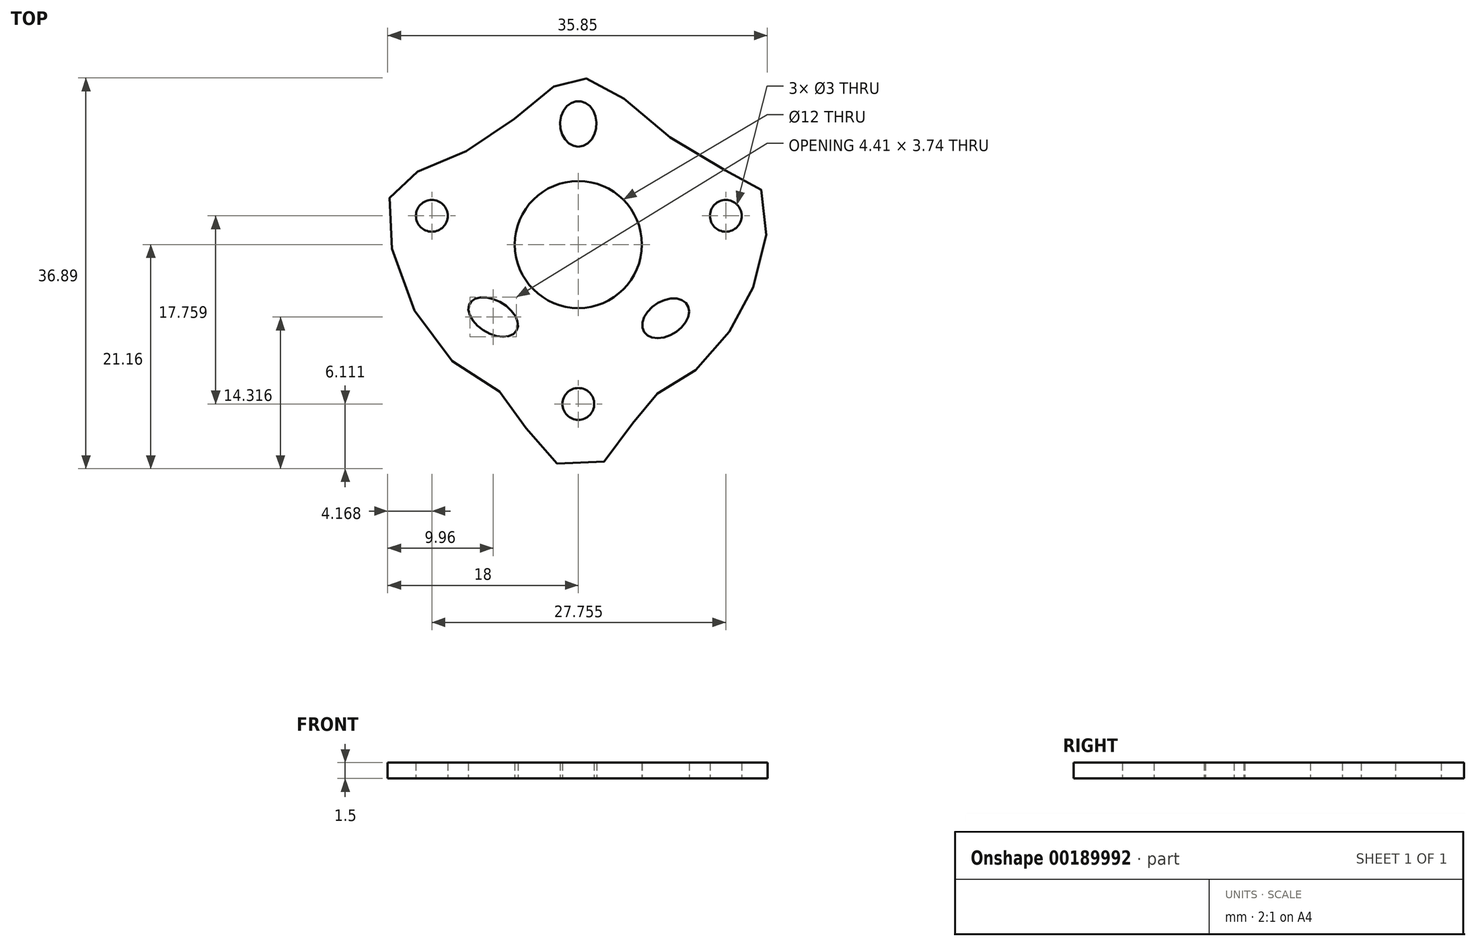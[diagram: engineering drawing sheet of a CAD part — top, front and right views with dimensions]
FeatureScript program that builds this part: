
annotation { "Feature Type Name" : "Feature", "Feature Type Description" : "" }
export const myFeature = defineFeature(function(context is Context, id is Id, definition is map)
    precondition{}
    {
        {
            var Q0;
            Q0=qCreatedBy(makeId("Top.planeOp"),FACE);
            var sketch = newSketch(context, id + "F0", { "sketchPlane" : qUnion([Q0])});
            skPoint(sketch, "E0", {"position": v(-6.76, 11.3) * mm});
            skPoint(sketch, "E1", {"position": v(-2.33, 14.92) * mm});
            skPoint(sketch, "E2", {"position": v(0, 15.73) * mm});
            skPoint(sketch, "E3", {"position": v(2.9, 14.82) * mm});
            skPoint(sketch, "E4", {"position": v(8.07, 10.55) * mm});
            skPoint(sketch, "E5", {"position": v(15.06, 6.46) * mm});
            skPoint(sketch, "E6", {"position": v(17.43, 4.91) * mm});
            skPoint(sketch, "E7", {"position": v(17.6, 0) * mm});
            skPoint(sketch, "E8", {"position": v(15.8, -5.62) * mm});
            skPoint(sketch, "E9", {"position": v(12.8, -10.07) * mm});
            skPoint(sketch, "E10", {"position": v(8.89, -13.43) * mm});
            skPoint(sketch, "E11", {"position": v(6.07, -14.98) * mm});
            skPoint(sketch, "E12", {"position": v(4.16, -18.89) * mm});
            skPoint(sketch, "E13", {"position": v(0, -21.16) * mm});
            skPoint(sketch, "E14", {"position": v(-4.16, -18.84) * mm});
            skPoint(sketch, "E15", {"position": v(-6.22, -14.9) * mm});
            skPoint(sketch, "E16", {"position": v(-11.24, -11.55) * mm});
            skPoint(sketch, "E17", {"position": v(-16.18, -4.71) * mm});
            skPoint(sketch, "E18", {"position": v(-18, 2.92) * mm});
            skPoint(sketch, "E19", {"position": v(-16.91, 5.91) * mm});
            skPoint(sketch, "E20", {"position": v(-12.73, 7.82) * mm});
            skPoint(sketch, "E21", {"position": v(13.92, 2.71) * mm});
            skPoint(sketch, "E22", {"position": v(-13.83, 2.71) * mm});
            skPoint(sketch, "E23", {"position": v(-8.04, -6.84) * mm});
            skPoint(sketch, "E24", {"position": v(8.25, -6.96) * mm});
            skPoint(sketch, "E25", {"position": v(0, -15.05) * mm});
            skPoint(sketch, "E26", {"position": v(0, 11.4) * mm});
            skFitSpline(sketch, "E27", {"points": [v(-2.33, 14.92) * mm, v(0, 15.73) * mm, v(2.9, 14.82) * mm, v(8.07, 10.55) * mm, v(15.06, 6.46) * mm, v(17.43, 4.91) * mm, v(17.6, 0) * mm, v(15.8, -5.62) * mm, v(12.8, -10.07) * mm, v(8.89, -13.43) * mm, v(6.07, -14.98) * mm, v(4.16, -18.89) * mm, v(0, -21.16) * mm, v(-4.16, -18.84) * mm, v(-6.22, -14.9) * mm, v(-11.24, -11.55) * mm, v(-16.18, -4.71) * mm, v(-18, 2.92) * mm, v(-16.91, 5.91) * mm, v(-12.73, 7.82) * mm, v(-6.76, 11.3) * mm, v(-2.33, 14.92) * mm]});
            skCircle(sketch, "E28", {"center": v(-13.83, 2.71) * mm, "radius": 1.5 * mm});
            skCircle(sketch, "E29", {"center": v(13.92, 2.71) * mm, "radius": 1.5 * mm});
            skCircle(sketch, "E30", {"center": v(0, -15.05) * mm, "radius": 1.5 * mm});
            skEllipse(sketch, "E31", {"center": v(-8.04, -6.84) * mm, "majorRadius": 2.56 * mm, "minorRadius": 1.55 * mm, "majorAxis": v(0.86, -0.5)});
            skEllipse(sketch, "E32", {"center": v(8.25, -6.96) * mm, "majorRadius": 2.42 * mm, "minorRadius": 1.61 * mm, "majorAxis": v(-0.84, -0.53)});
            skEllipse(sketch, "E33", {"center": v(0, 11.4) * mm, "majorRadius": 2.15 * mm, "minorRadius": 1.72 * mm, "majorAxis": v(0, -1)});
            skCircle(sketch, "E34", {"center": v(0, 0) * mm, "radius": 6 * mm});
            skSolve(sketch);
        }
        {
            var Q0;
            Q0 = qSketchRegion(id + "F0", true);
            extrude(context, id + "F1", {"entities" : qUnion([Q0]), "depth" : 1.5 * mm});
        }
    });
